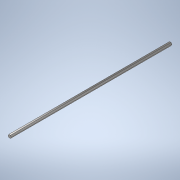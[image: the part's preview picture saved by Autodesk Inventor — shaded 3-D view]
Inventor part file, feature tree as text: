
AUTODESK INVENTOR PART (.ipt)
format: ipt  version: 2020 (Build 240168000, 168)  size: 108,032 bytes
history: native  units: in
note: dims shown in document units (in); Inventor stores cm internally (conversion verified against a paired STEP export)
features: extrude x1, sketch x1
ambient origin geometry x8: Origin, YZ Plane, XZ Plane, XY Plane, X Axis, Y Axis, Z Axis, Center Point
bodies: Solid1 (feature_tree)
feature tree (2):
  extrude  "Extrusion1"  Depth=29.0in TaperAngle=0.0deg
  sketch  "Sketch1"  dims[d0=0.5in d1=29.0in d2=0.0in]
